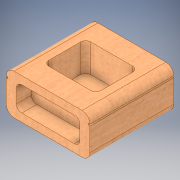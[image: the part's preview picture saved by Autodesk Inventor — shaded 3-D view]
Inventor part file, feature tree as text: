
AUTODESK INVENTOR PART (.ipt)
format: ipt  version: 2017 (Build 210142000, 142)  size: 191,488 bytes
history: native  units: in
note: dims shown in document units (in); Inventor stores cm internally (conversion verified against a paired STEP export)
features: sketch x6, extrude x5
ambient origin geometry x8: Origin, YZ Plane, XZ Plane, XY Plane, X Axis, Y Axis, Z Axis, Center Point
bodies: Solid1 (feature_tree)
feature tree (11):
  sketch  "Sketch1"  dims[d0=3.17in d1=1.53in]
  extrude  "Extrusion1"  Depth=1.53in
  extrude  "Extrusion2"  Depth=3.17in TaperAngle=0.0deg
  extrude  "Extrusion3"  Depth=0.93in
  extrude  "Extrusion4"  Depth=0.3in
  extrude  "Extrusion5"  Depth=0.57in TaperAngle=0.0deg
  sketch  "Sketch2"  dims[d2=0.3in d3=3.17in d4=0.0in]
  sketch  "Sketch3"  dims[d5=2.4in d6=0.93in]
  sketch  "Sketch4"  dims[d7=0.385in d8=0.3in]
  sketch  "Sketch5"  dims[d9=0.2in d10=0.57in d11=0.0in]
  sketch  "Sketch6"  dims[d12=1.98in d13=1.59in d14=0.82in d15=0.595in d16=1.07in d17=0.0in d18=0.2in d19=0.06in d20=0.06in d21=0.3in d22=3.17in d23=0.0in d24=0.06in d25=0.06in d26=3.17in d27=0.0in]
